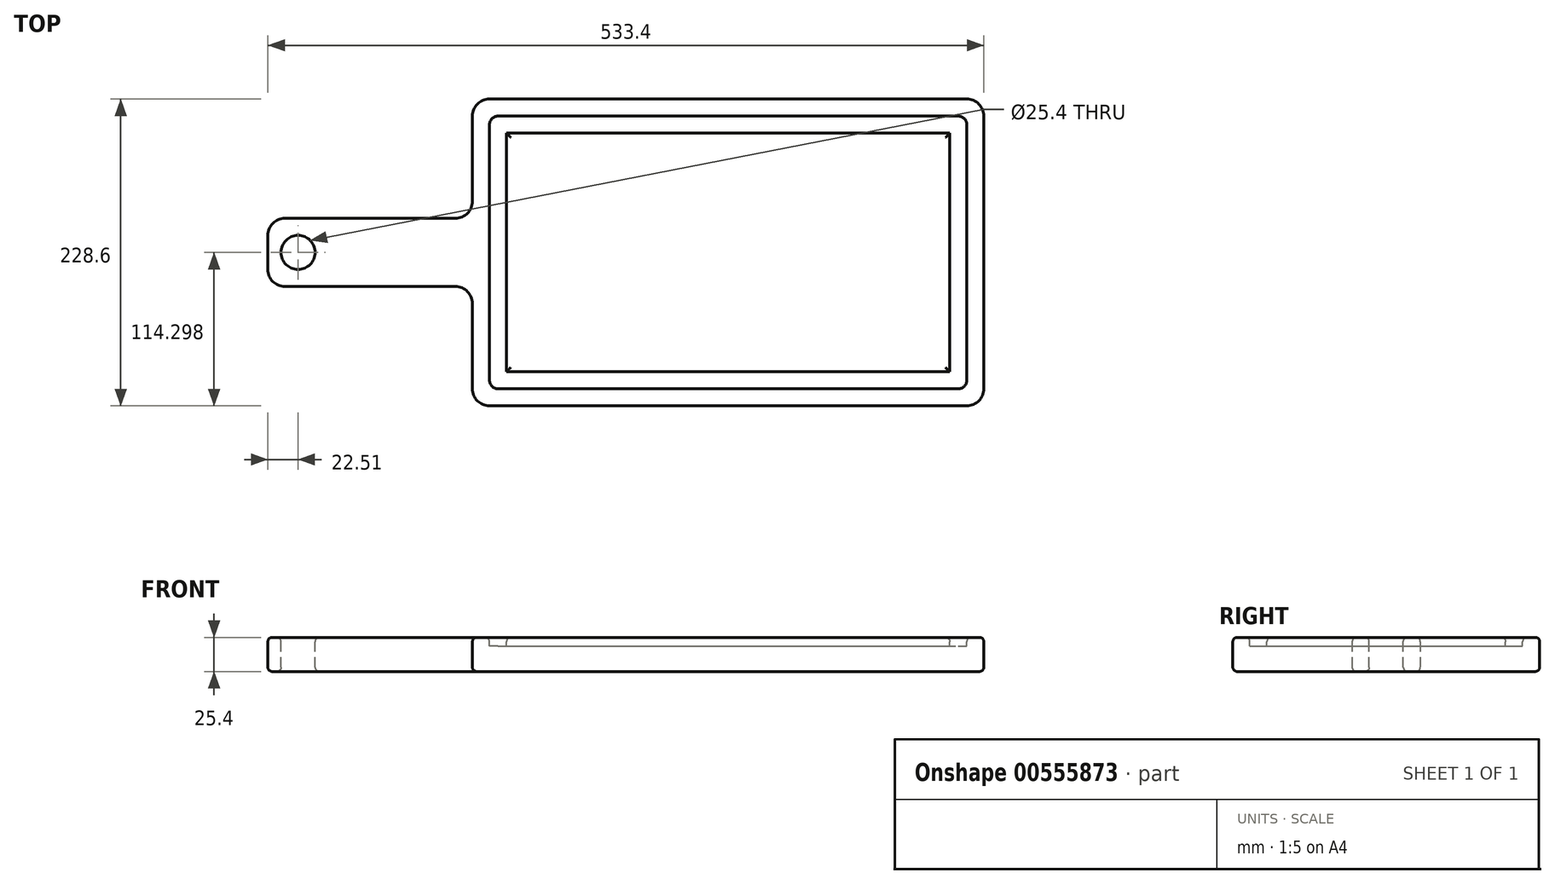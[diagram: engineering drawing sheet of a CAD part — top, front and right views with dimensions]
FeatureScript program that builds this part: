
annotation { "Feature Type Name" : "Feature", "Feature Type Description" : "" }
export const myFeature = defineFeature(function(context is Context, id is Id, definition is map)
    precondition{}
    {
        {
            var Q0;
            Q0=qCreatedBy(makeId("Top.planeOp"),FACE);
            var sketch = newSketch(context, id + "F0", { "sketchPlane" : qUnion([Q0])});
            skLineSegment(sketch, "E0.bottom", {"start": v(0, -8.16) * mm, "end": v(381, -8.16) * mm});
            skLineSegment(sketch, "E0.top", {"start": v(0, 220.44) * mm, "end": v(381, 220.44) * mm});
            skLineSegment(sketch, "E0.left", {"start": v(0, -8.16) * mm, "end": v(0, 220.44) * mm});
            skLineSegment(sketch, "E0.right", {"start": v(381, -8.16) * mm, "end": v(381, 220.44) * mm});
            skLineSegment(sketch, "E1.bottom", {"start": v(0, 131.54) * mm, "end": v(-152.4, 131.54) * mm});
            skLineSegment(sketch, "E1.top", {"start": v(0, 80.74) * mm, "end": v(-152.4, 80.74) * mm});
            skLineSegment(sketch, "E1.left", {"start": v(0, 131.54) * mm, "end": v(0, 80.74) * mm});
            skLineSegment(sketch, "E1.right", {"start": v(-152.4, 131.54) * mm, "end": v(-152.4, 80.74) * mm});
            skSolve(sketch);
        }
        {
            var Q0;
            {var subQ3=sQuery(id+"F0.wireOp",EDGE,"E0.bottom");Q0=makeQuery(id+"F0.imprint","IMPRINT",FACE,{"disambiguationData":[TD([[makeQuery(id+"F0.imprint","IMPRINT",EDGE,{"derivedFrom":subQ3}),1.0]])]});}
            var Q1;
            Q1=makeQuery(id+"F0.imprint","IMPRINT",FACE,{"disambiguationData":[TD([[makeQuery(id+"F0.imprint","IMPRINT",EDGE,{"derivedFrom":sQuery(id+"F0.wireOp",EDGE,"E1.bottom")}),1.0]])]});
            extrude(context, id + "F1", {"entities" : qUnion([Q0, Q1]), "depth" : 25.4 * mm, "offsetDistance" : 25.4 * mm});
        }
        {
            var Q0;
            Q0=makeQuery(id+"F1.opExtrude","CAP_FACE",FACE,{"disambiguationData":[OSD([sQuery(id+"F0.wireOp",EDGE,"E0.bottom"),sQuery(id+"F0.wireOp",EDGE,"E0.top"),sQuery(id+"F0.wireOp",EDGE,"E0.left"),sQuery(id+"F0.wireOp",EDGE,"E0.right"),sQuery(id+"F0.wireOp",EDGE,"E1.bottom"),sQuery(id+"F0.wireOp",EDGE,"E1.top"),sQuery(id+"F0.wireOp",EDGE,"E1.right")])],"isStart":false});
            var sketch = newSketch(context, id + "F2", { "sketchPlane" : qUnion([Q0])});
            skCircle(sketch, "E2", {"center": v(-129.9, 106.14) * mm, "radius": 12.7 * mm});
            skSolve(sketch);
        }
        {
            var Q0;
            Q0 = qSketchRegion(id + "F2", true);
            extrude(context, id + "F3", {"entities" : qUnion([Q0]), "operationType" : NewBodyOperationType.REMOVE, "oppositeDirection" : true, "depth" : 25.4 * mm, "offsetDistance" : 25.4 * mm});
        }
        {
            var Q0;
            Q0=makeQuery(id+"F1.opExtrude","CAP_FACE",FACE,{"disambiguationData":[OSD([sQuery(id+"F0.wireOp",EDGE,"E0.bottom"),sQuery(id+"F0.wireOp",EDGE,"E0.top"),sQuery(id+"F0.wireOp",EDGE,"E0.left"),sQuery(id+"F0.wireOp",EDGE,"E0.right"),sQuery(id+"F0.wireOp",EDGE,"E1.bottom"),sQuery(id+"F0.wireOp",EDGE,"E1.top"),sQuery(id+"F0.wireOp",EDGE,"E1.right")])],"isStart":false});
            var sketch = newSketch(context, id + "F4", { "sketchPlane" : qUnion([Q0])});
            skLineSegment(sketch, "E3.0", {"start": v(12.7, 4.54) * mm, "end": v(12.7, 80.74) * mm});
            skLineSegment(sketch, "E3.1", {"start": v(12.7, 131.54) * mm, "end": v(12.7, 207.74) * mm});
            skLineSegment(sketch, "E3.2", {"start": v(12.7, 207.74) * mm, "end": v(368.3, 207.74) * mm});
            skLineSegment(sketch, "E3.3", {"start": v(368.3, 4.54) * mm, "end": v(368.3, 207.74) * mm});
            skLineSegment(sketch, "E3.4", {"start": v(12.7, 4.54) * mm, "end": v(368.3, 4.54) * mm});
            skLineSegment(sketch, "E4", {"start": v(12.7, 131.54) * mm, "end": v(12.7, 80.74) * mm});
            skLineSegment(sketch, "E5.0", {"start": v(25.4, 131.54) * mm, "end": v(25.4, 195.04) * mm});
            skLineSegment(sketch, "E5.1", {"start": v(355.6, 17.24) * mm, "end": v(355.6, 195.04) * mm});
            skLineSegment(sketch, "E5.2", {"start": v(25.4, 17.24) * mm, "end": v(355.6, 17.24) * mm});
            skLineSegment(sketch, "E5.3", {"start": v(25.4, 195.04) * mm, "end": v(355.6, 195.04) * mm});
            skLineSegment(sketch, "E5.4", {"start": v(25.4, 17.24) * mm, "end": v(25.4, 80.74) * mm});
            skLineSegment(sketch, "E5.5", {"start": v(25.4, 131.54) * mm, "end": v(25.4, 80.74) * mm});
            skSolve(sketch);
        }
        {
            var Q0;
            Q0=makeQuery(id+"F4.imprint","IMPRINT",FACE,{"disambiguationData":[TD([[makeQuery(id+"F4.imprint","IMPRINT",EDGE,{"derivedFrom":sQuery(id+"F4.wireOp",EDGE,"E3.0")}),-1.0]])]});
            extrude(context, id + "F5", {"entities" : qUnion([Q0]), "operationType" : NewBodyOperationType.REMOVE, "oppositeDirection" : true, "depth" : 6.35 * mm, "offsetDistance" : 25.4 * mm});
        }
        {
            var Q0;
            Q0=makeQuery(id+"F5.boolean.opBoolean","COPY",EDGE,{"derivedFrom":makeQuery(id+"F5.opExtrude","SWEPT_EDGE",EDGE,{"disambiguationData":[OSD([sQuery(id+"F4.wireOp",EDGE,"E3.1"),sQuery(id+"F4.wireOp",EDGE,"E3.2")])]})});
            var Q1;
            Q1=makeQuery(id+"F5.boolean.opBoolean","COPY",EDGE,{"derivedFrom":makeQuery(id+"F5.opExtrude","SWEPT_EDGE",EDGE,{"disambiguationData":[OSD([sQuery(id+"F4.wireOp",EDGE,"E3.2"),sQuery(id+"F4.wireOp",EDGE,"E3.3")])]})});
            var Q2;
            Q2=makeQuery(id+"F5.boolean.opBoolean","COPY",EDGE,{"derivedFrom":makeQuery(id+"F5.opExtrude","SWEPT_EDGE",EDGE,{"disambiguationData":[OSD([sQuery(id+"F4.wireOp",EDGE,"E3.0"),sQuery(id+"F4.wireOp",EDGE,"E3.4")])]})});
            var Q3;
            Q3=makeQuery(id+"F5.boolean.opBoolean","COPY",EDGE,{"derivedFrom":makeQuery(id+"F5.opExtrude","SWEPT_EDGE",EDGE,{"disambiguationData":[OSD([sQuery(id+"F4.wireOp",EDGE,"E3.3"),sQuery(id+"F4.wireOp",EDGE,"E3.4")])]})});
            fillet(context, id + "F6", {"entities" : qUnion([Q0, Q1, Q2, Q3]), "radius" : 6.35 * mm, "tangentPropagation" : true, "allowEdgeOverflow" : false});
        }
        {
            var Q0;
            Q0=makeQuery(id+"F1.opExtrude","SWEPT_EDGE",EDGE,{"disambiguationData":[OSD([sQuery(id+"F0.wireOp",EDGE,"E0.bottom"),sQuery(id+"F0.wireOp",EDGE,"E0.left")])]});
            var Q1;
            Q1=makeQuery(id+"F1.opExtrude","SWEPT_EDGE",EDGE,{"disambiguationData":[OSD([sQuery(id+"F0.wireOp",EDGE,"E0.left"),sQuery(id+"F0.wireOp",EDGE,"E1.top"),sQuery(id+"F0.wireOp",EDGE,"E1.left")])]});
            var Q2;
            Q2=makeQuery(id+"F1.opExtrude","SWEPT_EDGE",EDGE,{"disambiguationData":[OSD([sQuery(id+"F0.wireOp",EDGE,"E1.top"),sQuery(id+"F0.wireOp",EDGE,"E1.right")])]});
            var Q3;
            Q3=makeQuery(id+"F1.opExtrude","SWEPT_EDGE",EDGE,{"disambiguationData":[OSD([sQuery(id+"F0.wireOp",EDGE,"E1.bottom"),sQuery(id+"F0.wireOp",EDGE,"E1.right")])]});
            var Q4;
            Q4=makeQuery(id+"F1.opExtrude","SWEPT_EDGE",EDGE,{"disambiguationData":[OSD([sQuery(id+"F0.wireOp",EDGE,"E0.left"),sQuery(id+"F0.wireOp",EDGE,"E1.bottom"),sQuery(id+"F0.wireOp",EDGE,"E1.left")])]});
            var Q5;
            Q5=makeQuery(id+"F1.opExtrude","SWEPT_EDGE",EDGE,{"disambiguationData":[OSD([sQuery(id+"F0.wireOp",EDGE,"E0.top"),sQuery(id+"F0.wireOp",EDGE,"E0.left")])]});
            var Q6;
            Q6=makeQuery(id+"F1.opExtrude","SWEPT_EDGE",EDGE,{"disambiguationData":[OSD([sQuery(id+"F0.wireOp",EDGE,"E0.top"),sQuery(id+"F0.wireOp",EDGE,"E0.right")])]});
            var Q7;
            Q7=makeQuery(id+"F1.opExtrude","SWEPT_EDGE",EDGE,{"disambiguationData":[OSD([sQuery(id+"F0.wireOp",EDGE,"E0.bottom"),sQuery(id+"F0.wireOp",EDGE,"E0.right")])]});
            fillet(context, id + "F7", {"entities" : qUnion([Q0, Q1, Q2, Q3, Q4, Q5, Q6, Q7]), "radius" : 12.7 * mm, "tangentPropagation" : true, "allowEdgeOverflow" : false});
        }
        {
            var Q0;
            Q0=makeQuery(id+"F5.boolean.opBoolean","SPLIT",FACE,{"disambiguationData":[TD([makeQuery(id+"F5.opExtrude","SWEPT_FACE",FACE,{"disambiguationData":[OSD([sQuery(id+"F4.wireOp",EDGE,"E5.1")])]})])],"derivedFrom":makeQuery(id+"F1.opExtrude","CAP_FACE",FACE,{"disambiguationData":[OSD([sQuery(id+"F0.wireOp",EDGE,"E0.bottom"),sQuery(id+"F0.wireOp",EDGE,"E0.top"),sQuery(id+"F0.wireOp",EDGE,"E0.left"),sQuery(id+"F0.wireOp",EDGE,"E0.right"),sQuery(id+"F0.wireOp",EDGE,"E1.bottom"),sQuery(id+"F0.wireOp",EDGE,"E1.top"),sQuery(id+"F0.wireOp",EDGE,"E1.right")])],"isStart":false})});
            var Q1;
            {var subQ0=sQuery(id+"F0.wireOp",EDGE,"E1.right");var subQ1=sQuery(id+"F0.wireOp",EDGE,"E1.top");var subQ2=sQuery(id+"F0.wireOp",EDGE,"E1.bottom");var subQ3=sQuery(id+"F0.wireOp",EDGE,"E0.right");var subQ4=sQuery(id+"F0.wireOp",EDGE,"E0.bottom");var subQ5=sQuery(id+"F0.wireOp",EDGE,"E0.left");var subQ6=sQuery(id+"F0.wireOp",EDGE,"E0.top");Q1=makeQuery(id+"F5.boolean.opBoolean","SPLIT",FACE,{"disambiguationData":[TD([makeQuery(id+"F1.opExtrude","SWEPT_FACE",FACE,{"disambiguationData":[OSD([subQ4])]})])],"derivedFrom":makeQuery(id+"F1.opExtrude","CAP_FACE",FACE,{"disambiguationData":[OSD([subQ4,subQ6,subQ5,subQ3,subQ2,subQ1,subQ0])],"isStart":false})});}
            var Q2;
            Q2=makeQuery(id+"F1.opExtrude","CAP_FACE",FACE,{"disambiguationData":[OSD([sQuery(id+"F0.wireOp",EDGE,"E0.bottom"),sQuery(id+"F0.wireOp",EDGE,"E0.top"),sQuery(id+"F0.wireOp",EDGE,"E0.left"),sQuery(id+"F0.wireOp",EDGE,"E0.right"),sQuery(id+"F0.wireOp",EDGE,"E1.bottom"),sQuery(id+"F0.wireOp",EDGE,"E1.top"),sQuery(id+"F0.wireOp",EDGE,"E1.right")])],"isStart":true});
            fillet(context, id + "F8", {"entities" : qUnion([Q0, Q1, Q2]), "radius" : 3.17 * mm, "tangentPropagation" : true, "allowEdgeOverflow" : false});
        }
    });
